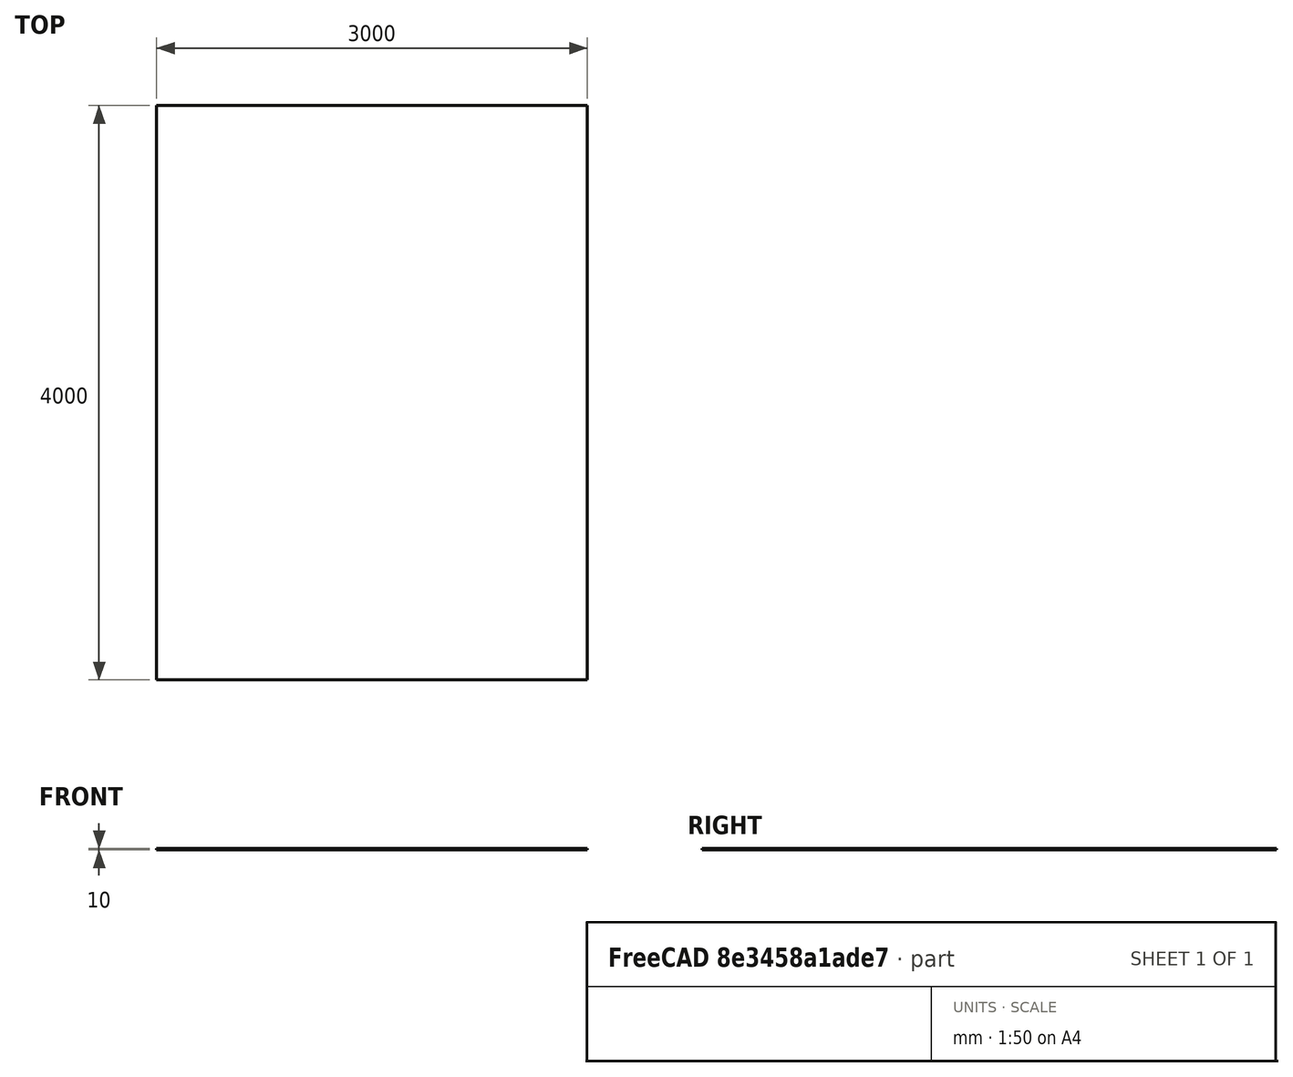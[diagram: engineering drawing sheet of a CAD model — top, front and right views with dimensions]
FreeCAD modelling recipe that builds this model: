
FCSTD DOCUMENT  (FreeCAD 0.15R4671 (Git))
Label: Sol
License: All rights reserved
LicenseURL: http://en.wikipedia.org/wiki/All_rights_reserved
objects: Sketcher::SketchObject×1, PartDesign::Pad×1
note: 3 computed .brp shape members not serialized (recipe doc carries the construction recipe); baked Part::Feature solids carry a one-line shape summary decoded from their .brp

FEATURE [Sketcher::SketchObject] Sketch
  sketch-geometry (4):
    g0: LineSegment StartX=-1500 StartY=2000 StartZ=0 EndX=1500 EndY=2000 EndZ=0
    g1: LineSegment StartX=1500 StartY=2000 StartZ=0 EndX=1500 EndY=-2000 EndZ=0
    g2: LineSegment StartX=1500 StartY=-2000 StartZ=0 EndX=-1500 EndY=-2000 EndZ=0
    g3: LineSegment StartX=-1500 StartY=-2000 StartZ=0 EndX=-1500 EndY=2000 EndZ=0
  constraints (12):
    c: Coincident(g0,g1)
    c: Coincident(g1,g2)
    c: Coincident(g2,g3)
    c: Coincident(g3,g0)
    c: Horizontal(g0)
    c: Horizontal(g2)
    c: Vertical(g1)
    c: Vertical(g3)
    c: Distance(g1) = 4000
    c: Distance(g0) = 3000
    c: Symmetric(g0,g0,g-2)
    c: Symmetric(g0,g2,g-1)
FEATURE [PartDesign::Pad] Pad
  Length = 10
  Length2 = 100
  Reversed = true
  Sketch = -> Sketch
  Type = 0
